# Revit family: Подвесной пластинчатый рекуператор LITENED REP
name_source: partatom
category: Оборудование
revit_build: Autodesk Revit 2017 (Build: 20160225_1515(x64)
units: mm (PartAtom-declared; Revit-internal decimal feet)

## family parameters
Всегда вертикально = Да
На основе рабочей плоскости = Нет
Общий = Нет
При загрузке вырезать с полостями = Нет
Размер круглого соединителя = Использовать диаметр
Тип детали = Нормальный
Точка расчета площади = Нет

## types (5) — shared parameters
Диаметр патрубков = 16 мм
Единица измерения = шт.
Завод изготовитель = NED
Ключевая пометка = Вентиляция
Наименование и тех.хар-ка = Подвесной пластинчатый рекуператор
Раздел = ОВ
высота ножек = 10 мм

## per-type parameters (varying)
| type | А | А1 | Б | Б1 | Г | Д | Д1 | Масса единицы | Материал | Середина | Тип, марка, обозначение | размер В |
| 50-25 | 1725 мм | 1705 мм | 470 мм | 450 мм | 395 мм | 1065 мм | 1045 мм | 108 | Сталь серая | 235 мм | LITENED 50-25 REP | 1650 мм |
| 50-30 | 1725 мм | 1705 мм | 520 мм | 500 мм | 445 мм | 1065 мм | 1045 мм | 110 | Сталь серая | 260 мм | LITENED 50-30 REP | 1650 мм |
| 60-30 | 1925 мм | 1905 мм | 520 мм | 500 мм | 445 мм | 1205 мм | 1185 мм | 135 | Сталь серая | 260 мм | LITENED 60-30 REP | 1850 мм |
| 60-35 | 1925 мм | 1905 мм | 570 мм | 550 мм | 495 мм | 1205 мм | 1185 мм | 141 | Сталь серая | 285 мм | LITENED 60-35 REP | 1850 мм |
| 70-40 | 2125 мм | 2105 мм | 620 мм | 600 мм | 545 мм | 1265 мм | 1245 мм | 150 | RAL 0000 Серый металл | 310 мм | LITENED 70-40 REP | 2050 мм |
